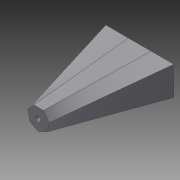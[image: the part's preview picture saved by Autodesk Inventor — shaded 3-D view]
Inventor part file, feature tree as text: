
AUTODESK INVENTOR PART (.ipt)
format: ipt  version: 2015 (Build 190159000, 159)  size: 108,032 bytes
history: native  units: in
note: dims shown in document units (in); Inventor stores cm internally (conversion verified against a paired STEP export)
features: sketch x3, plane x1, loft x1, hole x1
ambient origin geometry x8: Origin, YZ Plane, XZ Plane, XY Plane, X Axis, Y Axis, Z Axis, Center Point
bodies: Solid1 (feature_tree)
feature tree (6):
  sketch  "Sketch1"  dims[d0=2.0in d1=0.0in d2=90.0deg]
  plane  "Work Plane1"
  loft  "Loft1"
  hole  "Hole1"  [1 undecoded]
  sketch  "Sketch3"  dims[d7=0.07in d8=0.25in d9=0.1in d10=0.25in d11=0.5635in d12=0.375in d13=0.8108in]
  sketch  "Sketch2"  dims[d3=0.0in d4=90.0deg d5=1.0in d6=1.0in]
note: 1 required parameter value undecoded (feature->parameter linkage not recoverable at this tier; creation-order binding heuristic only, values carry confidence <= 0.55)
